# Revit family: LC + 280 types Sans hôte
name_source: partatom
category: Dispositifs d'éclairage
units: mm (PartAtom-declared; Revit-internal decimal feet)

## family parameters
Basée sur le plan de construction = Non
Conserver l'orientation des annotations = Non
Cote de connecteur circulaire = Utiliser le diamètre
Couper avec des vides une fois chargée = Non
Partagée = Non
Point de calcul de pièce = Non
Toujours verticalement = Oui
Type d'élément = Normal

## types (3) — shared parameters
Classe = II
Code d'assemblage = D5010200
Elévation par défaut = 250 cm
Fabricant = B.E.G.
Hauteur de montage max = 300 cm
IP = 44
Image du type = MURAL.JPG
Marque = LUXOMAT
Mode de pose = Mural
Position en hauteur = 250 cm
Température ambiante = -25°C à + 50°C
URL = http://www.luxomat.com

## per-type parameters (varying)
| type | Alimentation | Charge Cos ɸ =0.5 | Charge Cos ɸ =1 | Charge LED | Commentaires du type | Consommation | Modèle | Relais | Référence | Type de Sortie |
| 01- LC + 280 Générique | 110-240 V AC |  |  |  | DET.MOUV.280°/16M MURAL |  | LC + 280 |  |  |  |
| 02- LC + 280 réf 91008 | 110-240 V AC | 1000 VA | 2000 W | 250 W | DET.MOUV.1 CONTACT.280°/16M MURAL | 0.24 W | LC + 280 | 8.7 A | 91008 | TOR |
| 03- LC + 280 DALISYS réf 93308 | 10 à 22 V DC par BUS DALI | 0 | 0 | 0 | MULTI.CAPTEUR.MOUV.DALISYS.280°/16M MURAL | 7 mA | LC + 280 DALISYS | 0 | 93308 | DALI Adressable |
